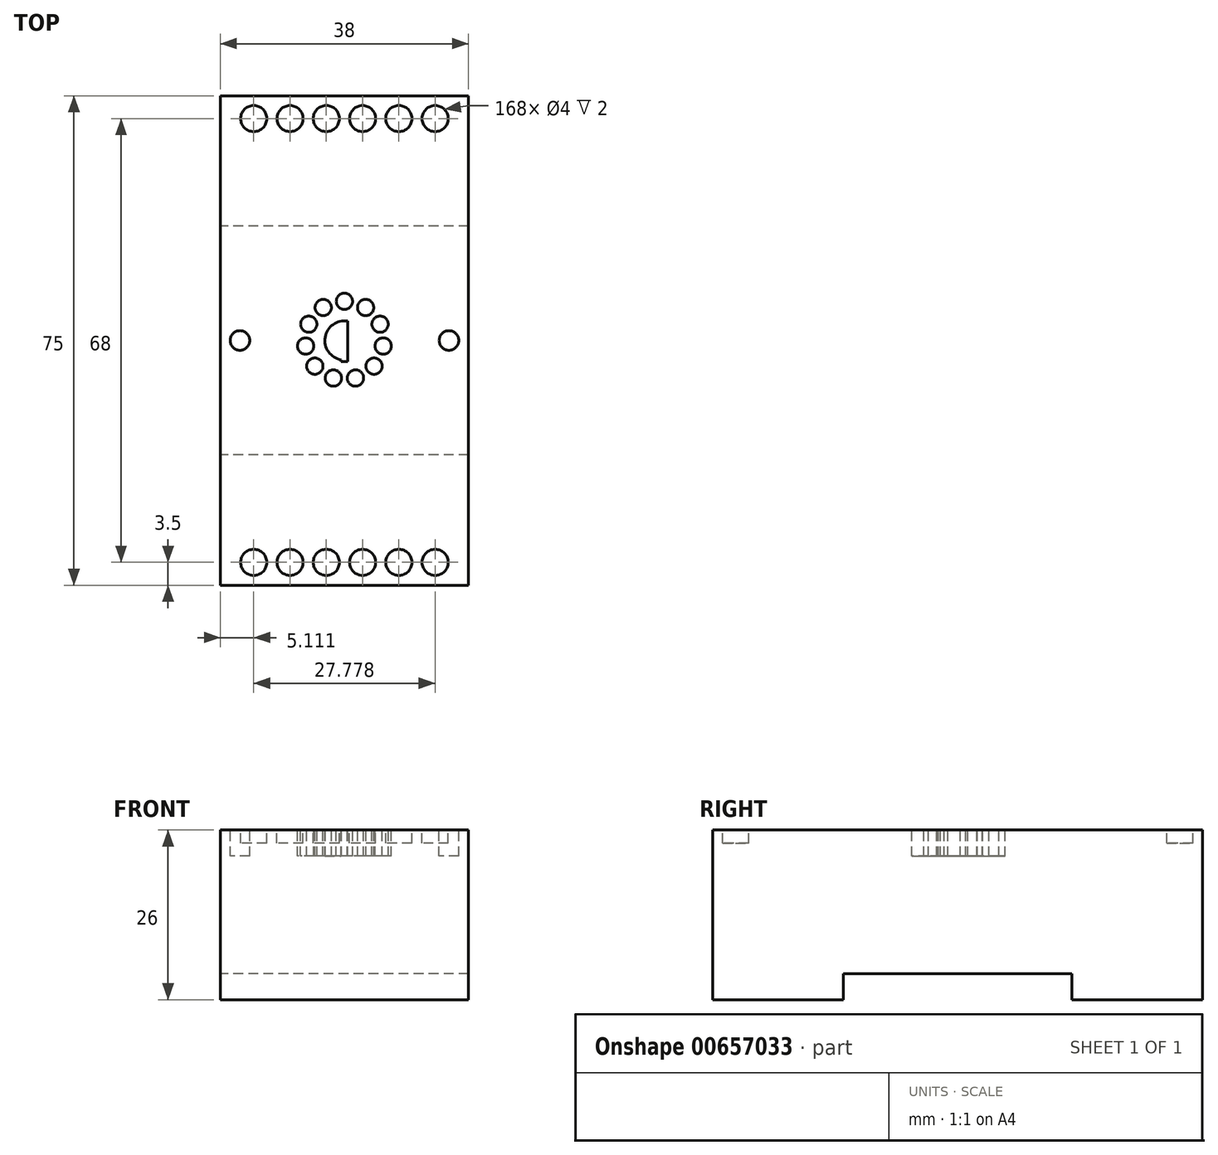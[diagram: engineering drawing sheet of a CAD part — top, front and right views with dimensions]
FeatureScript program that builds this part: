
annotation { "Feature Type Name" : "Feature", "Feature Type Description" : "" }
export const myFeature = defineFeature(function(context is Context, id is Id, definition is map)
    precondition{}
    {
        {
            var Q0;
            Q0=qCreatedBy(makeId("Right.planeOp"),FACE);
            var sketch = newSketch(context, id + "F0", { "sketchPlane" : qUnion([Q0])});
            skLineSegment(sketch, "E0", {"start": v(0, 0) * mm, "end": v(20, 0) * mm});
            skLineSegment(sketch, "E1", {"start": v(20, 0) * mm, "end": v(20, 4) * mm});
            skLineSegment(sketch, "E2", {"start": v(20, 4) * mm, "end": v(55, 4) * mm});
            skLineSegment(sketch, "E3", {"start": v(55, 4) * mm, "end": v(55, 0) * mm});
            skLineSegment(sketch, "E4", {"start": v(55, 0) * mm, "end": v(75, 0) * mm});
            skLineSegment(sketch, "E5", {"start": v(75, 0) * mm, "end": v(75, 26) * mm});
            skLineSegment(sketch, "E6", {"start": v(75, 26) * mm, "end": v(0, 26) * mm});
            skLineSegment(sketch, "E7", {"start": v(0, 26) * mm, "end": v(0, 0) * mm});
            skSolve(sketch);
        }
        {
            var Q0;
            Q0=makeQuery(id+"F0.imprint","IMPRINT",FACE,{"disambiguationData":[TD([[makeQuery(id+"F0.imprint","IMPRINT",EDGE,{"derivedFrom":sQuery(id+"F0.wireOp",EDGE,"E0")}),1.0]])]});
            extrude(context, id + "F1", {"entities" : qUnion([Q0]), "depth" : 38 * mm, "offsetDistance" : 25 * mm});
        }
        {
            var Q0;
            Q0=makeQuery(id+"F1.opExtrude","SWEPT_FACE",FACE,{"disambiguationData":[OSD([sQuery(id+"F0.wireOp",EDGE,"E6")])]});
            var sketch = newSketch(context, id + "F2", { "sketchPlane" : qUnion([Q0])});
            skCircle(sketch, "E8", {"center": v(3, 37.5) * mm, "radius": 1.5 * mm});
            skPoint(sketch, "E8.centerSnap0", {"position": v(0, 37.5) * mm});
            skCircle(sketch, "E9", {"center": v(35, 37.5) * mm, "radius": 1.5 * mm});
            skCircle(sketch, "E10", {"center": v(19, 37.5) * mm, "radius": 3 * mm});
            skPoint(sketch, "E10.centerSnap0", {"position": v(19, 75) * mm});
            skLineSegment(sketch, "E11.bottom", {"start": v(19.5, 34.25) * mm, "end": v(18.5, 34.25) * mm});
            skLineSegment(sketch, "E11.top", {"start": v(19.5, 40.75) * mm, "end": v(18.5, 40.75) * mm});
            skLineSegment(sketch, "E11.left", {"start": v(19.5, 34.25) * mm, "end": v(19.5, 40.75) * mm});
            skLineSegment(sketch, "E11.right", {"start": v(18.5, 34.25) * mm, "end": v(18.5, 40.75) * mm});
            skCircle(sketch, "E12", {"center": v(19, 43.5) * mm, "radius": 1.25 * mm});
            skPoint(sketch, "E12.centerSnap0", {"position": v(19, 34.25) * mm});
            skCircle(sketch, "E13.1.0", {"center": v(15.76, 42.55) * mm, "radius": 1.25 * mm});
            skCircle(sketch, "E13.2.0", {"center": v(13.54, 40) * mm, "radius": 1.25 * mm});
            skCircle(sketch, "E13.3.0", {"center": v(13.06, 36.65) * mm, "radius": 1.25 * mm});
            skCircle(sketch, "E13.4.0", {"center": v(14.47, 33.57) * mm, "radius": 1.25 * mm});
            skCircle(sketch, "E13.5.0", {"center": v(17.3, 31.74) * mm, "radius": 1.25 * mm});
            skCircle(sketch, "E13.6.0", {"center": v(20.7, 31.74) * mm, "radius": 1.25 * mm});
            skCircle(sketch, "E13.7.0", {"center": v(23.53, 33.57) * mm, "radius": 1.25 * mm});
            skCircle(sketch, "E13.8.0", {"center": v(24.94, 36.65) * mm, "radius": 1.25 * mm});
            skCircle(sketch, "E13.9.0", {"center": v(24.46, 40) * mm, "radius": 1.25 * mm});
            skCircle(sketch, "E13.10.0", {"center": v(22.24, 42.55) * mm, "radius": 1.25 * mm});
            skLineSegment(sketch, "E13.anchor1", {"start": v(19, 37.5) * mm, "end": v(19, 43.5) * mm, "construction": true});
            skLineSegment(sketch, "E13.anchor2", {"start": v(19, 37.5) * mm, "end": v(22.24, 42.55) * mm, "construction": true});
            skSolve(sketch);
        }
        {
            var Q0;
            {var subQ0=sQuery(id+"F2.wireOp",EDGE,"E11.right");var subQ1=sQuery(id+"F2.wireOp",EDGE,"E10");var subQ2=makeQuery(id+"F2.imprint","INTERSECT",VERTEX,{"disambiguationData":[OD(0.0)],"derivedFrom":[subQ1,subQ0]});Q0=makeQuery(id+"F2.imprint","IMPRINT",FACE,{"disambiguationData":[TD([[makeQuery(id+"F2.imprint","IMPRINT",EDGE,{"disambiguationData":[TD([[subQ2,-1.0]])],"derivedFrom":subQ1}),1.0]])]});}
            var Q1;
            {var subQ0=sQuery(id+"F2.wireOp",EDGE,"E11.right");var subQ1=sQuery(id+"F2.wireOp",EDGE,"E10");var subQ2=makeQuery(id+"F2.imprint","INTERSECT",VERTEX,{"disambiguationData":[OD(0.0)],"derivedFrom":[subQ1,subQ0]});Q1=makeQuery(id+"F2.imprint","IMPRINT",FACE,{"disambiguationData":[TD([[makeQuery(id+"F2.imprint","IMPRINT",EDGE,{"disambiguationData":[TD([[subQ2,1.0]])],"derivedFrom":subQ1}),1.0]])]});}
            var Q2;
            {var subQ0=sQuery(id+"F2.wireOp",EDGE,"E11.left");var subQ1=sQuery(id+"F2.wireOp",EDGE,"E10");var subQ2=makeQuery(id+"F2.imprint","INTERSECT",VERTEX,{"disambiguationData":[OD(0.0)],"derivedFrom":[subQ1,subQ0]});Q2=makeQuery(id+"F2.imprint","IMPRINT",FACE,{"disambiguationData":[TD([[makeQuery(id+"F2.imprint","IMPRINT",EDGE,{"disambiguationData":[TD([[subQ2,1.0]])],"derivedFrom":subQ1}),1.0]])]});}
            var Q3;
            {var subQ5=sQuery(id+"F2.wireOp",EDGE,"E11.bottom");Q3=makeQuery(id+"F2.imprint","IMPRINT",FACE,{"disambiguationData":[TD([[makeQuery(id+"F2.imprint","IMPRINT",EDGE,{"derivedFrom":subQ5}),-1.0]])]});}
            var Q4;
            Q4=makeQuery(id+"F2.imprint","IMPRINT",FACE,{"disambiguationData":[TD([[makeQuery(id+"F2.imprint","IMPRINT",EDGE,{"derivedFrom":sQuery(id+"F2.wireOp",EDGE,"E12")}),1.0]])]});
            var Q5;
            Q5=makeQuery(id+"F2.imprint","IMPRINT",FACE,{"disambiguationData":[TD([[makeQuery(id+"F2.imprint","IMPRINT",EDGE,{"derivedFrom":sQuery(id+"F2.wireOp",EDGE,"E9")}),1.0]])]});
            var Q6;
            Q6=makeQuery(id+"F2.imprint","IMPRINT",FACE,{"disambiguationData":[TD([[makeQuery(id+"F2.imprint","IMPRINT",EDGE,{"derivedFrom":sQuery(id+"F2.wireOp",EDGE,"E8")}),1.0]])]});
            var Q7;
            Q7=makeQuery(id+"F2.imprint","IMPRINT",FACE,{"disambiguationData":[TD([[makeQuery(id+"F2.imprint","IMPRINT",EDGE,{"derivedFrom":sQuery(id+"F2.wireOp",EDGE,"E13.1.0")}),1.0]])]});
            var Q8;
            Q8=makeQuery(id+"F2.imprint","IMPRINT",FACE,{"disambiguationData":[TD([[makeQuery(id+"F2.imprint","IMPRINT",EDGE,{"derivedFrom":sQuery(id+"F2.wireOp",EDGE,"E13.2.0")}),1.0]])]});
            var Q9;
            Q9=makeQuery(id+"F2.imprint","IMPRINT",FACE,{"disambiguationData":[TD([[makeQuery(id+"F2.imprint","IMPRINT",EDGE,{"derivedFrom":sQuery(id+"F2.wireOp",EDGE,"E13.3.0")}),1.0]])]});
            var Q10;
            Q10=makeQuery(id+"F2.imprint","IMPRINT",FACE,{"disambiguationData":[TD([[makeQuery(id+"F2.imprint","IMPRINT",EDGE,{"derivedFrom":sQuery(id+"F2.wireOp",EDGE,"E13.4.0")}),1.0]])]});
            var Q11;
            Q11=makeQuery(id+"F2.imprint","IMPRINT",FACE,{"disambiguationData":[TD([[makeQuery(id+"F2.imprint","IMPRINT",EDGE,{"derivedFrom":sQuery(id+"F2.wireOp",EDGE,"E13.5.0")}),1.0]])]});
            var Q12;
            Q12=makeQuery(id+"F2.imprint","IMPRINT",FACE,{"disambiguationData":[TD([[makeQuery(id+"F2.imprint","IMPRINT",EDGE,{"derivedFrom":sQuery(id+"F2.wireOp",EDGE,"E13.6.0")}),1.0]])]});
            var Q13;
            Q13=makeQuery(id+"F2.imprint","IMPRINT",FACE,{"disambiguationData":[TD([[makeQuery(id+"F2.imprint","IMPRINT",EDGE,{"derivedFrom":sQuery(id+"F2.wireOp",EDGE,"E13.7.0")}),1.0]])]});
            var Q14;
            Q14=makeQuery(id+"F2.imprint","IMPRINT",FACE,{"disambiguationData":[TD([[makeQuery(id+"F2.imprint","IMPRINT",EDGE,{"derivedFrom":sQuery(id+"F2.wireOp",EDGE,"E13.8.0")}),1.0]])]});
            var Q15;
            Q15=makeQuery(id+"F2.imprint","IMPRINT",FACE,{"disambiguationData":[TD([[makeQuery(id+"F2.imprint","IMPRINT",EDGE,{"derivedFrom":sQuery(id+"F2.wireOp",EDGE,"E13.9.0")}),1.0]])]});
            var Q16;
            Q16=makeQuery(id+"F2.imprint","IMPRINT",FACE,{"disambiguationData":[TD([[makeQuery(id+"F2.imprint","IMPRINT",EDGE,{"derivedFrom":sQuery(id+"F2.wireOp",EDGE,"E13.10.0")}),1.0]])]});
            extrude(context, id + "F3", {"entities" : qUnion([Q0, Q1, Q2, Q3, Q4, Q5, Q6, Q7, Q8, Q9, Q10, Q11, Q12, Q13, Q14, Q15, Q16]), "operationType" : NewBodyOperationType.REMOVE, "oppositeDirection" : true, "depth" : 4 * mm, "offsetDistance" : 25 * mm});
        }
        {
            var Q0;
            Q0=makeQuery(id+"F1.opExtrude","SWEPT_FACE",FACE,{"disambiguationData":[OSD([sQuery(id+"F0.wireOp",EDGE,"E6")])]});
            var sketch = newSketch(context, id + "F4", { "sketchPlane" : qUnion([Q0])});
            skCircle(sketch, "E14", {"center": v(5.11, 71.5) * mm, "radius": 2 * mm});
            skCircle(sketch, "E15.1.0.0", {"center": v(10.67, 71.5) * mm, "radius": 2 * mm});
            skCircle(sketch, "E15.2.0.0", {"center": v(16.22, 71.5) * mm, "radius": 2 * mm});
            skCircle(sketch, "E15.3.0.0", {"center": v(21.78, 71.5) * mm, "radius": 2 * mm});
            skCircle(sketch, "E15.4.0.0", {"center": v(27.33, 71.5) * mm, "radius": 2 * mm});
            skCircle(sketch, "E15.5.0.0", {"center": v(32.89, 71.5) * mm, "radius": 2 * mm});
            skLineSegment(sketch, "E15.direction1", {"start": v(5.11, 71.5) * mm, "end": v(10.67, 71.5) * mm, "construction": true});
            skCircle(sketch, "E16", {"center": v(5.11, 3.5) * mm, "radius": 2 * mm});
            skCircle(sketch, "E17.1.0.0", {"center": v(10.67, 3.5) * mm, "radius": 2 * mm});
            skCircle(sketch, "E17.2.0.0", {"center": v(16.22, 3.5) * mm, "radius": 2 * mm});
            skCircle(sketch, "E17.3.0.0", {"center": v(21.78, 3.5) * mm, "radius": 2 * mm});
            skCircle(sketch, "E17.4.0.0", {"center": v(27.33, 3.5) * mm, "radius": 2 * mm});
            skCircle(sketch, "E17.5.0.0", {"center": v(32.89, 3.5) * mm, "radius": 2 * mm});
            skLineSegment(sketch, "E17.direction1", {"start": v(5.11, 3.5) * mm, "end": v(10.67, 3.5) * mm, "construction": true});
            skSolve(sketch);
        }
        {
            var Q0;
            Q0 = qSketchRegion(id + "F4", true);
            extrude(context, id + "F5", {"entities" : qUnion([Q0]), "operationType" : NewBodyOperationType.REMOVE, "oppositeDirection" : true, "depth" : 2 * mm, "offsetDistance" : 25 * mm});
        }
    });
